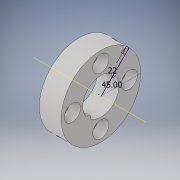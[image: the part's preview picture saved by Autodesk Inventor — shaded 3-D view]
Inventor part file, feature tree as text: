
AUTODESK INVENTOR PART (.ipt)
format: ipt  version: 2019 (Build 230136000, 136)  size: 171,520 bytes
history: native  units: in
note: dims shown in document units (in); Inventor stores cm internally (conversion verified against a paired STEP export)
features: sketch x5, extrude x4, plane x2, pattern_circular x1, thread x1, mirror x1
ambient origin geometry x8: Origin, YZ Plane, XZ Plane, XY Plane, X Axis, Y Axis, Z Axis, Center Point
bodies: Solid1 (feature_tree)
feature tree (14):
  extrude  "Extrusion1"  Depth=1.7323in
  extrude  "Extrusion3"  Depth=1.2402in
  extrude  "Extrusion4"  Depth=1.1811in TaperAngle=0.0deg
  pattern_circular  "Circular Pattern1"  Count=4 Angle=360.0deg
  sketch  "Sketch6"  dims[d16=0.3937in d17=45.0deg d18=0.1181in]
  plane  "Work Plane1"
  extrude  "Extrusion5"  TaperAngle=45.0deg  [1 undecoded]
  plane  "Work Plane2"
  thread  "Thread1"  [1 undecoded]
  mirror  "Mirror1"
  sketch  "Sketch2"  dims[d3=0.7874in d4=1.7323in]
  sketch  "Sketch4"  dims[d5=0.4724in d6=0.0in d9=1.2402in]
  sketch  "Sketch5"  dims[d10=0.2008in d11=1.1811in d12=0.0in d13=1.5748in d14=360.0deg]
  sketch  "Sketch7"  dims[d19=45.0deg d20=0.3543in d21=0.2362in d22=0.0in d23=0.8661in d24=45.0deg d25=0.2047in d26=0.3937in d27=0.0in d28=0.3937in d29=0.0in]
note: 2 required parameter values undecoded (feature->parameter linkage not recoverable at this tier; creation-order binding heuristic only, values carry confidence <= 0.55)
